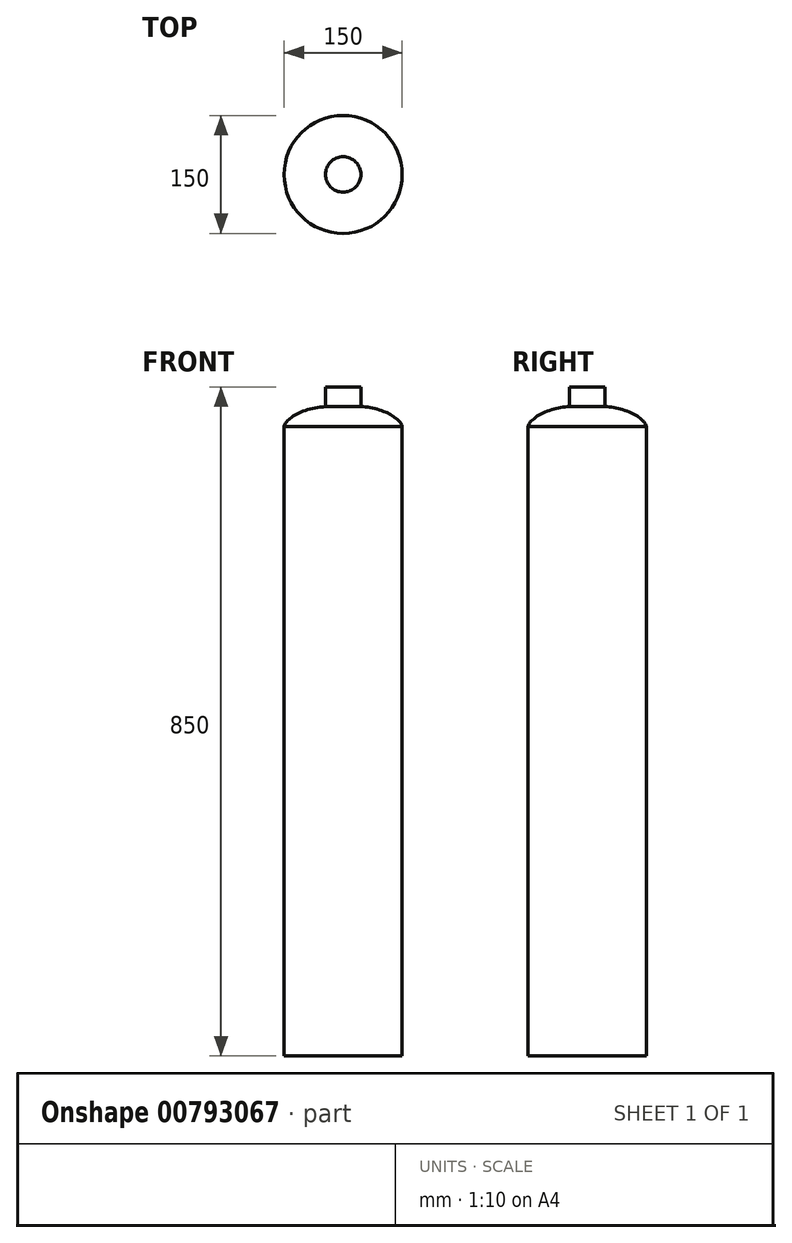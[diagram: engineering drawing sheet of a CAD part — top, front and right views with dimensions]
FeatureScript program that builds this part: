
annotation { "Feature Type Name" : "Feature", "Feature Type Description" : "" }
export const myFeature = defineFeature(function(context is Context, id is Id, definition is map)
    precondition{}
    {
        {
            var Q0;
            Q0=qCreatedBy(makeId("Front.planeOp"),FACE);
            var sketch = newSketch(context, id + "F0", { "sketchPlane" : qUnion([Q0])});
            skLineSegment(sketch, "E0", {"start": v(0, -53.42) * mm, "end": v(-75, -53.42) * mm});
            skLineSegment(sketch, "E1", {"start": v(-75, -53.42) * mm, "end": v(-75, 746.58) * mm});
            skLineSegment(sketch, "E2", {"start": v(-75, 746.58) * mm, "end": v(0, 746.58) * mm});
            skLineSegment(sketch, "E3", {"start": v(0, 746.58) * mm, "end": v(0, 771.58) * mm});
            skLineSegment(sketch, "E4", {"start": v(0, 771.58) * mm, "end": v(0, 796.58) * mm});
            skLineSegment(sketch, "E5", {"start": v(0, 771.58) * mm, "end": v(-22.5, 771.58) * mm});
            skLineSegment(sketch, "E6", {"start": v(-22.5, 771.58) * mm, "end": v(-22.5, 796.58) * mm});
            skLineSegment(sketch, "E7", {"start": v(-22.5, 796.58) * mm, "end": v(0, 796.58) * mm});
            skFitSpline(sketch, "E8", {"points": [v(-75, 746.58) * mm, v(-22.5, 771.58) * mm], "startDerivative": vector(7, 31.72) * mm, "endDerivative": vector(77.92, 2.1) * mm});
            skLineSegment(sketch, "E9", {"start": v(0, 841.72) * mm, "end": v(0, -95.56) * mm});
            skLineSegment(sketch, "E10", {"start": v(0, 841.72) * mm, "end": v(0, -78.32) * mm});
            skSolve(sketch);
        }
        {
            var Q0;
            {var subQ0=sQuery(id+"F0.wireOp",EDGE,"E0");Q0=makeQuery(id+"F0.imprint","IMPRINT",FACE,{"disambiguationData":[TD([[makeQuery(id+"F0.imprint","IMPRINT",EDGE,{"derivedFrom":subQ0}),-1.0]])]});}
            var Q1;
            {var subQ0=sQuery(id+"F0.wireOp",EDGE,"E2");Q1=makeQuery(id+"F0.imprint","IMPRINT",FACE,{"disambiguationData":[TD([[makeQuery(id+"F0.imprint","IMPRINT",EDGE,{"derivedFrom":subQ0}),1.0]])]});}
            var Q2;
            {var subQ0=sQuery(id+"F0.wireOp",EDGE,"E5");Q2=makeQuery(id+"F0.imprint","IMPRINT",FACE,{"disambiguationData":[TD([[makeQuery(id+"F0.imprint","IMPRINT",EDGE,{"derivedFrom":subQ0}),-1.0]])]});}
            var Q3;
            Q3=sQuery(id+"F0.wireOp",EDGE,"E0");
            var Q4;
            Q4=sQuery(id+"F0.wireOp",EDGE,"E1");
            var Q5;
            Q5=sQuery(id+"F0.wireOp",EDGE,"E8");
            var Q6;
            Q6=sQuery(id+"F0.wireOp",EDGE,"E6");
            var Q7;
            Q7=sQuery(id+"F0.wireOp",EDGE,"E7");
            var Q8;
            Q8=sQuery(id+"F0.wireOp",EDGE,"E10");
            revolve(context, id + "F1", {"bodyType" : ToolBodyType.SURFACE, "surfaceOperationType" : NewSurfaceOperationType.NEW, "entities" : qUnion([Q0, Q1, Q2]), "surfaceEntities" : qUnion([Q3, Q4, Q5, Q6, Q7]), "axis" : qUnion([Q8]), "revolveType" : RevolveType.FULL});
        }
    });
